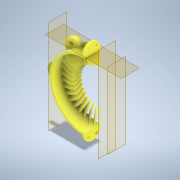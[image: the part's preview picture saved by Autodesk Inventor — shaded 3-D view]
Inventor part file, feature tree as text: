
AUTODESK INVENTOR PART (.ipt)
format: ipt  version: 2021.2 (Build 252289000, 289)  size: 1,584,128 bytes
history: native  units: in
note: dims shown in document units (in); Inventor stores cm internally (conversion verified against a paired STEP export)
features: sketch x11, extrude x10, plane x4, pattern_circular x3, fillet x2, loft x1, other x1
ambient origin geometry x8: Origin, YZ Plane, XZ Plane, XY Plane, X Axis, Y Axis, Z Axis, Center Point
bodies: Solid1 (feature_tree)
feature tree (32):
  extrude  "Extrusion1"  Depth=4.25in
  plane  "Work Plane1"
  plane  "Work Plane2"
  extrude  "Extrusion3"  Depth=1.0in
  fillet  "Fillet1"  Radius=2.125in
  extrude  "Extrusion4"  TaperAngle=0.0deg  [1 undecoded]
  pattern_circular  "Circular Pattern2"  Count=2 Angle=360.0deg
  plane  "Work Plane3"
  extrude  "Extrusion5"  Depth=1.0in
  extrude  "Extrusion6"  Depth=0.5in
  fillet  "Fillet2"  [1 undecoded]
  extrude  "Extrusion7"  Depth=0.5in TaperAngle=0.0deg
  pattern_circular  "Circular Pattern3"  [2 undecoded]
  extrude  "Extrusion8"  Depth=0.25in
  plane  "Work Plane4"
  loft  "Loft1"
  pattern_circular  "Circular Pattern5"  [2 undecoded]
  extrude  "Extrusion9"  Depth=2.3622in TaperAngle=360.0deg
  extrude  "Extrusion10"  Depth=0.25in
  extrude  "Extrusion11"  Depth=0.125in
  sketch  "Sketch1"  dims[d0=4.0in d1=4.25in]
  sketch  "Sketch3"  dims[d2=1.0in d3=0.0in d4=1.5in d10=2.125in]
  sketch  "Sketch4"  dims[d11=0.25in d12=0.0in]
  sketch  "Sketch5"  dims[d13=0.5in d14=0.0in]
  sketch  "Sketch6"  dims[d15=0.5in]
  sketch  "Sketch7"  dims[d16=0.125in]
  sketch  "Sketch8"  dims[d17=0.2in]
  sketch  "Sketch9"  dims[d18=0.5in d19=0.0in d20=0.7874in d21=360.0deg]
  other  "Edges1"
  sketch  "Sketch10"  dims[d23=-2.125in d24=1.0in]
  sketch  "Sketch11"  dims[d25=0.25in d26=0.5in d27=0.0in]
  sketch  "Sketch12"  dims[d28=0.1in d29=0.0in d30=0.5in d31=0.0in d32=0.5in d33=0.25in d34=0.2in d35=0.5in d36=0.0in d37=2.3622in d38=360.0deg d40=0.25in d41=0.125in d42=0.25in d43=0.2in d49=0.5in d50=0.0312in d51=0.5in d52=0.0in d56=0.9in d57=0.0in d58=90.0deg d59=0.0in d60=90.0deg d61=14.1732in d62=360.0deg d64=2.2625in d65=0.0in d66=0.0777in d67=0.0in d68=0.0in d69=0.8in d70=0.0in d71=0.5in d72=0.0344in]
note: 6 required parameter values undecoded (feature->parameter linkage not recoverable at this tier; creation-order binding heuristic only, values carry confidence <= 0.55)
